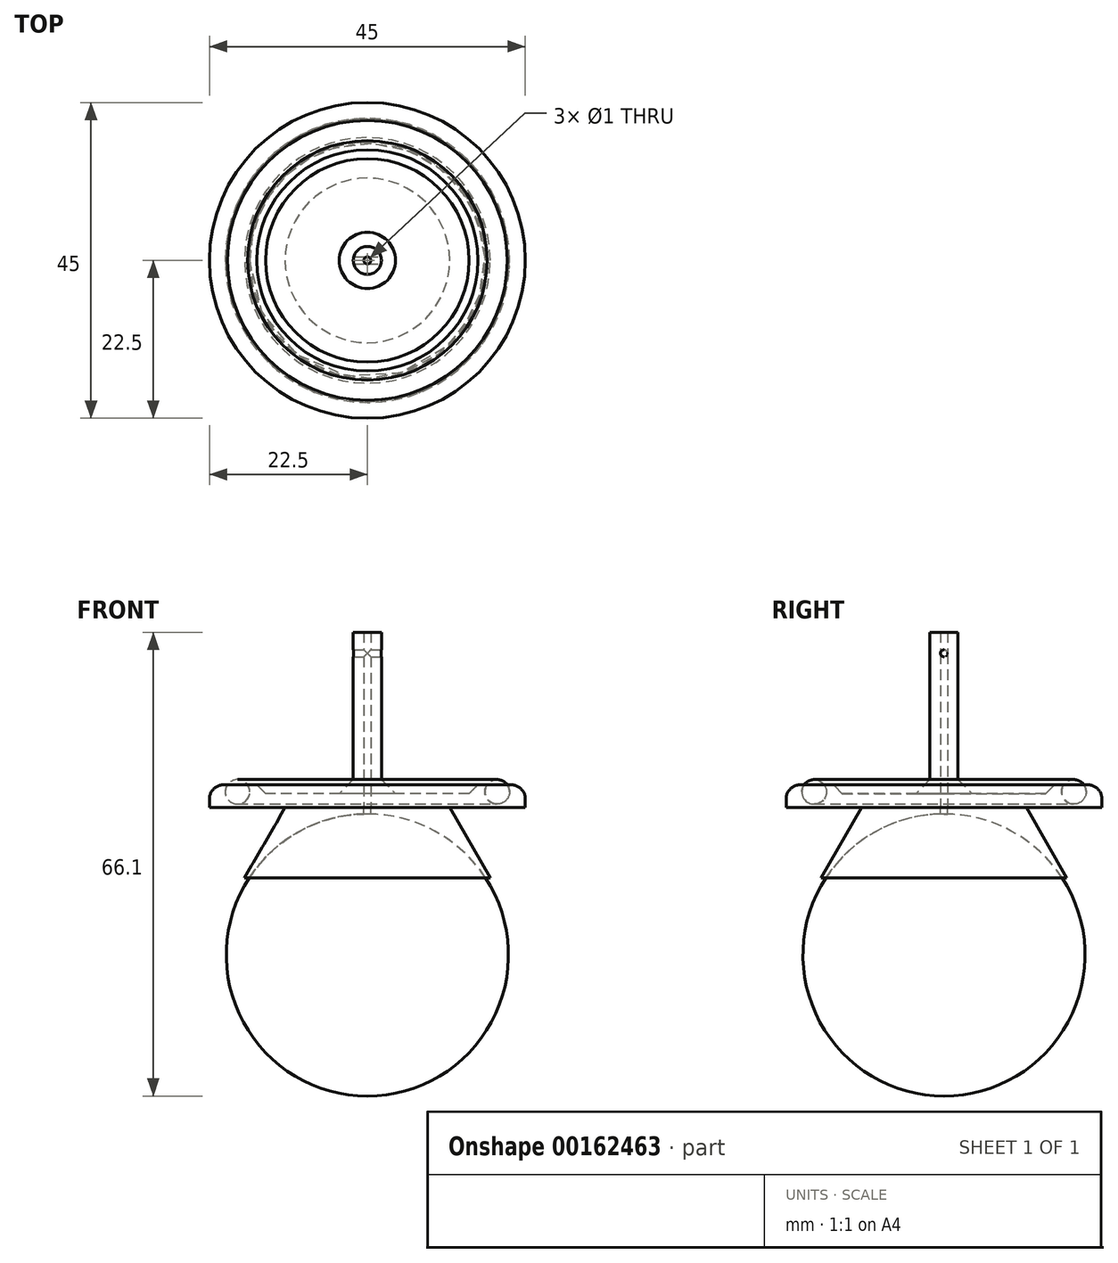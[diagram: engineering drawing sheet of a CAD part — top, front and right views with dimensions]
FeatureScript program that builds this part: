
annotation { "Feature Type Name" : "Feature", "Feature Type Description" : "" }
export const myFeature = defineFeature(function(context is Context, id is Id, definition is map)
    precondition{}
    {
        {
            var Q0;
            Q0=qCreatedBy(makeId("Top.planeOp"),FACE);
            var sketch = newSketch(context, id + "F0", { "sketchPlane" : qUnion([Q0])});
            skCircle(sketch, "E0", {"center": v(0, 0) * mm, "radius": 22.5 * mm});
            skCircle(sketch, "E1", {"center": v(0, 0) * mm, "radius": 2 * mm});
            skCircle(sketch, "E2", {"center": v(0, 0) * mm, "radius": 16.5 * mm});
            skCircle(sketch, "E3", {"center": v(0, 0) * mm, "radius": 0.5 * mm});
            skSolve(sketch);
        }
        {
            var Q0;
            Q0=makeQuery(id+"F0.imprint","IMPRINT",FACE,{"disambiguationData":[TD([[makeQuery(id+"F0.imprint","IMPRINT",EDGE,{"derivedFrom":sQuery(id+"F0.wireOp",EDGE,"E1")}),-1.0]])]});
            var Q1;
            Q1=makeQuery(id+"F0.imprint","IMPRINT",FACE,{"disambiguationData":[TD([[makeQuery(id+"F0.imprint","IMPRINT",EDGE,{"derivedFrom":sQuery(id+"F0.wireOp",EDGE,"E0")}),1.0]])]});
            var Q2;
            Q2=makeQuery(id+"F0.imprint","IMPRINT",FACE,{"disambiguationData":[TD([[makeQuery(id+"F0.imprint","IMPRINT",EDGE,{"derivedFrom":sQuery(id+"F0.wireOp",EDGE,"E1")}),1.0]])]});
            extrude(context, id + "F1", {"entities" : qUnion([Q0, Q1, Q2]), "depth" : 2 * mm});
        }
        {
            var Q0;
            Q0=makeQuery(id+"F0.imprint","IMPRINT",FACE,{"disambiguationData":[TD([[makeQuery(id+"F0.imprint","IMPRINT",EDGE,{"derivedFrom":sQuery(id+"F0.wireOp",EDGE,"E1")}),1.0]])]});
            extrude(context, id + "F2", {"entities" : qUnion([Q0]), "operationType" : NewBodyOperationType.ADD, "depth" : 25 * mm});
        }
        {
            var Q0;
            Q0=makeQuery(id+"F0.imprint","IMPRINT",FACE,{"disambiguationData":[TD([[makeQuery(id+"F0.imprint","IMPRINT",EDGE,{"derivedFrom":sQuery(id+"F0.wireOp",EDGE,"E0")}),1.0]])]});
            extrude(context, id + "F3", {"entities" : qUnion([Q0]), "operationType" : NewBodyOperationType.ADD, "depth" : (0.5 + 3.5 - 0.75) * mm});
        }
        {
            var Q0;
            Q0=makeQuery(id+"F1.opExtrude","CAP_FACE",FACE,{"disambiguationData":[OSD([sQuery(id+"F0.wireOp",EDGE,"E0")])],"isStart":true});
            cPlane(context, id + "F4", {"entities" : qUnion([Q0]), "cplaneType" : CPlaneType.OFFSET, "offset" : (0.5 + 3.5 / 2) * mm, "oppositeDirection" : true, "width" : 150 * mm, "height" : 150 * mm});
        }
        {
            var Q0;
            Q0=qCreatedBy(id+"F4.planeOp",FACE);
            var sketch = newSketch(context, id + "F5", { "sketchPlane" : qUnion([Q0])});
            skCircle(sketch, "E4", {"center": v(0, 0) * mm, "radius": 18.5 * mm});
            skSolve(sketch);
        }
        {
            var Q0;
            Q0=qCreatedBy(makeId("Right.planeOp"),FACE);
            var sketch = newSketch(context, id + "F6", { "sketchPlane" : qUnion([Q0])});
            skCircle(sketch, "E5", {"center": v(-18.5, 2.25) * mm, "radius": 1.75 * mm});
            skSolve(sketch);
        }
        {
            var Q0;
            Q0=makeQuery(id+"F6.imprint","IMPRINT",FACE,{"disambiguationData":[TD([[makeQuery(id+"F6.imprint","IMPRINT",EDGE,{"derivedFrom":sQuery(id+"F6.wireOp",EDGE,"E5")}),1.0]])]});
            var Q1;
            Q1=sQuery(id+"F5.wireOp",EDGE,"E4");
            revolve(context, id + "F7", {"entities" : qUnion([Q0]), "axis" : qUnion([Q1]), "revolveType" : RevolveType.FULL, "oppositeDirection" : true});
        }
        {
            var Q0;
            Q0=makeQuery(id+"F7.opRevolve","SWEPT_BODY",BODY,{"disambiguationData":[OSD([sQuery(id+"F6.wireOp",EDGE,"E5")])]});
            var Q1;
            Q1=makeQuery(id+"F1.opExtrude","SWEPT_BODY",BODY,{"disambiguationData":[OSD([sQuery(id+"F0.wireOp",EDGE,"E0")])]});
            booleanBodies(context, id + "F8", {"operationType" : BooleanOperationType.SUBTRACTION, "tools" : qUnion([Q0]), "targets" : qUnion([Q1]), "keepTools" : true});
        }
        {
            var Q0;
            Q0=makeQuery(id+"F2.boolean.opBoolean","INTERSECT",EDGE,{"derivedFrom":[makeQuery(id+"F1.opExtrude","CAP_FACE",FACE,{"disambiguationData":[OSD([sQuery(id+"F0.wireOp",EDGE,"E0")])],"isStart":false}),makeQuery(id+"F2.opExtrude","SWEPT_FACE",FACE,{"disambiguationData":[OSD([sQuery(id+"F0.wireOp",EDGE,"E1")])]})]});
            var Q1;
            Q1=makeQuery(id+"F3.boolean.opBoolean","INTERSECT",EDGE,{"derivedFrom":[makeQuery(id+"F1.opExtrude","CAP_FACE",FACE,{"disambiguationData":[OSD([sQuery(id+"F0.wireOp",EDGE,"E0")])],"isStart":false}),makeQuery(id+"F3.opExtrude","SWEPT_FACE",FACE,{"disambiguationData":[OSD([sQuery(id+"F0.wireOp",EDGE,"E2")])]})]});
            chamfer(context, id + "F9", {"entities" : qUnion([Q0, Q1]), "width" : 2 * mm, "tangentPropagation" : true});
        }
        {
            var Q0;
            Q0=makeQuery(id+"F3.opExtrude","CAP_EDGE",EDGE,{"disambiguationData":[OSD([sQuery(id+"F0.wireOp",EDGE,"E0")])],"isStart":false});
            fillet(context, id + "F10", {"entities" : qUnion([Q0]), "radius" : 2 * mm, "tangentPropagation" : true, "allowEdgeOverflow" : false});
        }
        {
            var Q0;
            Q0=makeQuery(id+"F1.opExtrude","CAP_FACE",FACE,{"disambiguationData":[OSD([sQuery(id+"F0.wireOp",EDGE,"E0")])],"isStart":true});
            var sketch = newSketch(context, id + "F11", { "sketchPlane" : qUnion([Q0])});
            skCircle(sketch, "E6.0", {"center": v(0, 0) * mm, "radius": 17.5 * mm});
            skCircle(sketch, "E7", {"center": v(0, 0) * mm, "radius": 0.5 * mm});
            skSolve(sketch);
        }
        {
            var Q0;
            Q0 = qSketchRegion(id + "F11", true);
            extrude(context, id + "F12", {"entities" : qUnion([Q0]), "depth" : 10 * mm});
        }
        {
            var Q0;
            Q0=qCreatedBy(makeId("Right.planeOp"),FACE);
            var sketch = newSketch(context, id + "F13", { "sketchPlane" : qUnion([Q0])});
            skCircle(sketch, "E8", {"center": v(0, -21) * mm, "radius": 20.1 * mm});
            skLineSegment(sketch, "E9", {"start": v(0, -21) * mm, "end": v(0, 0) * mm});
            skLineSegment(sketch, "E10", {"start": v(0, -21) * mm, "end": v(0, -41.1) * mm});
            skSolve(sketch);
        }
        {
            var Q0;
            {var subQ0=sQuery(id+"F13.wireOp",EDGE,"E10");Q0=makeQuery(id+"F13.imprint","IMPRINT",FACE,{"disambiguationData":[TD([[makeQuery(id+"F13.imprint","IMPRINT",EDGE,{"derivedFrom":subQ0}),-1.0]])]});}
            var Q1;
            Q1=sQuery(id+"F13.wireOp",EDGE,"E9");
            revolve(context, id + "F14", {"entities" : qUnion([Q0]), "axis" : qUnion([Q1]), "revolveType" : RevolveType.FULL, "oppositeDirection" : true});
        }
        {
            var Q0;
            Q0=makeQuery(id+"F12.opExtrude","CAP_EDGE",EDGE,{"disambiguationData":[OSD([sQuery(id+"F11.wireOp",EDGE,"E6.0")])],"isStart":true});
            chamfer(context, id + "F15", {"entities" : qUnion([Q0]), "chamferType" : ChamferType.OFFSET_ANGLE, "width" : 10 * mm, "oppositeDirection" : false, "angle" : 30 * degree, "tangentPropagation" : true});
        }
        {
            var Q0;
            Q0=makeQuery(id+"F14.opRevolve","SWEPT_BODY",BODY,{"disambiguationData":[OSD([sQuery(id+"F13.wireOp",EDGE,"E8"),sQuery(id+"F13.wireOp",EDGE,"E9"),sQuery(id+"F13.wireOp",EDGE,"E10")])]});
            var Q1;
            Q1=makeQuery(id+"F12.opExtrude","SWEPT_BODY",BODY,{"disambiguationData":[OSD([sQuery(id+"F11.wireOp",EDGE,"E6.0")])]});
            booleanBodies(context, id + "F16", {"operationType" : BooleanOperationType.SUBTRACTION, "tools" : qUnion([Q0]), "targets" : qUnion([Q1]), "keepTools" : true});
        }
        {
            var Q0;
            Q0=qCreatedBy(makeId("Right.planeOp"),FACE);
            var sketch = newSketch(context, id + "F17", { "sketchPlane" : qUnion([Q0])});
            skPoint(sketch, "E11", {"position": v(0, 22) * mm});
            skCircle(sketch, "E12", {"center": v(0, 22) * mm, "radius": 0.5 * mm});
            skSolve(sketch);
        }
        {
            var Q0;
            Q0=makeQuery(id+"F17.imprint","IMPRINT",FACE,{"disambiguationData":[TD([[makeQuery(id+"F17.imprint","IMPRINT",EDGE,{"derivedFrom":sQuery(id+"F17.wireOp",EDGE,"E12")}),1.0]])]});
            var Q1;
            Q1=sQuery(id+"F17.wireOp",EDGE,"E12");
            extrude(context, id + "F18", {"entities" : qUnion([Q0]), "operationType" : NewBodyOperationType.REMOVE, "surfaceEntities" : qUnion([Q1]), "oppositeDirection" : true, "depth" : 25 * mm, "symmetric" : true});
        }
    });
